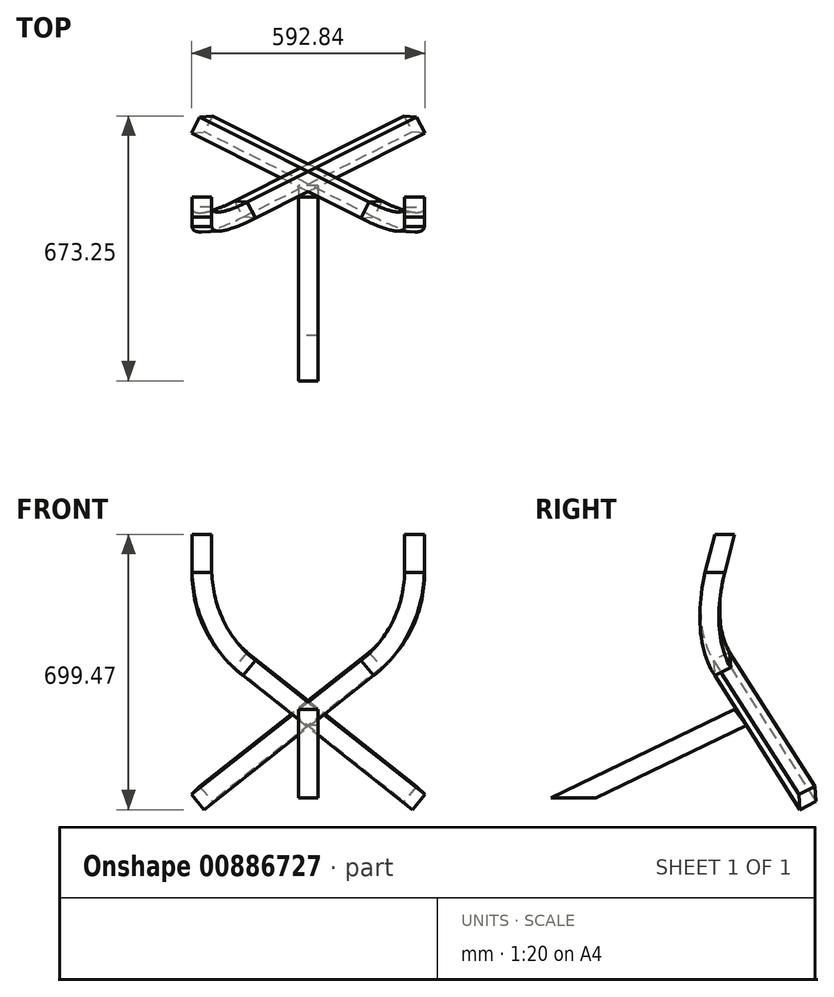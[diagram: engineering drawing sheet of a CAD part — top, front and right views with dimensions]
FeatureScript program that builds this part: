
annotation { "Feature Type Name" : "Feature", "Feature Type Description" : "" }
export const myFeature = defineFeature(function(context is Context, id is Id, definition is map)
    precondition{}
    {
        {
            var Q0;
            Q0=qCreatedBy(makeId("Top.planeOp"),FACE);
            var sketch = newSketch(context, id + "F0", { "sketchPlane" : qUnion([Q0])});
            skPoint(sketch, "E0", {"position": v(270, -243.58) * mm});
            skPoint(sketch, "E1", {"position": v(270, 136.42) * mm});
            skPoint(sketch, "E2", {"position": v(270, -73.58) * mm});
            skLineSegment(sketch, "E3", {"start": v(0, 0) * mm, "end": v(0, 375.12) * mm});
            skPoint(sketch, "E4.MirrorP", {"position": v(-270, 136.42) * mm});
            skPoint(sketch, "E5.MirrorP", {"position": v(-270, -73.58) * mm});
            skPoint(sketch, "E6.MirrorP", {"position": v(-270, -243.58) * mm});
            skLineSegment(sketch, "E7.bottom", {"start": v(-295, 111.42) * mm, "end": v(-245, 111.42) * mm});
            skLineSegment(sketch, "E7.top", {"start": v(-295, 161.42) * mm, "end": v(-245, 161.42) * mm});
            skLineSegment(sketch, "E7.left", {"start": v(-295, 111.42) * mm, "end": v(-295, 161.42) * mm});
            skLineSegment(sketch, "E7.right", {"start": v(-245, 111.42) * mm, "end": v(-245, 161.42) * mm});
            skPoint(sketch, "E8", {"position": v(0, -400) * mm});
            skSolve(sketch);
        }
        {
            var Q0;
            Q0=qCreatedBy(makeId("Top.planeOp"),FACE);
            cPlane(context, id + "F1", {"entities" : qUnion([Q0]), "cplaneType" : CPlaneType.OFFSET, "offset" : 670 * mm, "width" : 150 * mm, "height" : 150 * mm});
        }
        {
            var Q0;
            Q0=qCreatedBy(id+"F1.planeOp",FACE);
            var sketch = newSketch(context, id + "F2", { "sketchPlane" : qUnion([Q0])});
            skPoint(sketch, "E9.0", {"position": v(270, -73.58) * mm});
            skPoint(sketch, "E10.0", {"position": v(-270, -73.58) * mm});
            skLineSegment(sketch, "E11.bottom", {"start": v(245, -48.58) * mm, "end": v(295, -48.58) * mm});
            skLineSegment(sketch, "E11.top", {"start": v(245, -98.58) * mm, "end": v(295, -98.58) * mm});
            skLineSegment(sketch, "E11.left", {"start": v(245, -48.58) * mm, "end": v(245, -98.58) * mm});
            skLineSegment(sketch, "E11.right", {"start": v(295, -48.58) * mm, "end": v(295, -98.58) * mm});
            skSolve(sketch);
        }
        {
            var Q0;
            Q0=sQuery(id+"F0.wireOp",VERTEX,"E0");
            var Q1;
            Q1=sQuery(id+"F0.wireOp",VERTEX,"E4.MirrorP");
            var Q2;
            Q2=sQuery(id+"F2.wireOp",VERTEX,"E9.0");
            cPlane(context, id + "F3", {"entities" : qUnion([Q0, Q1, Q2]), "cplaneType" : CPlaneType.THREE_POINT, "offset" : 25 * mm, "width" : 150 * mm, "height" : 150 * mm});
        }
        {
            var Q0;
            Q0=qCreatedBy(id+"F3.planeOp",FACE);
            var sketch = newSketch(context, id + "F4", { "sketchPlane" : qUnion([Q0])});
            skPoint(sketch, "E12.0", {"position": v(-297.57, 33.55) * mm});
            skPoint(sketch, "E13.0", {"position": v(356.09, 631.33) * mm});
            skPoint(sketch, "E14.0", {"position": v(356.09, -59.9) * mm});
            skLineSegment(sketch, "E15", {"start": v(-297.57, 33.55) * mm, "end": v(223.46, 310.6) * mm});
            skLineSegment(sketch, "E16", {"start": v(356.09, 531.33) * mm, "end": v(356.09, 631.33) * mm});
            skPoint(sketch, "E17.visualSharp", {"position": v(356.09, 381.11) * mm});
            skArc(sketch, "E17.filletArc", {"start": v(223.46, 310.6) * mm, "mid": v(320.38, 402.57) * mm, "end": v(356.09, 531.33) * mm});
            skSolve(sketch);
        }
        {
            var Q0;
            Q0=makeQuery(id+"F2.imprint","IMPRINT",FACE,{"disambiguationData":[TD([[makeQuery(id+"F2.imprint","IMPRINT",EDGE,{"derivedFrom":sQuery(id+"F2.wireOp",EDGE,"E11.bottom")}),-1.0]])]});
            var Q1;
            Q1=sQuery(id+"F4.wireOp",EDGE,"E16");
            var Q2;
            Q2=sQuery(id+"F4.wireOp",EDGE,"E17.filletArc");
            var Q3;
            Q3=sQuery(id+"F4.wireOp",EDGE,"E15");
            sweep(context, id + "F5", {"profiles" : qUnion([Q0]), "path" : qUnion([Q1, Q2, Q3])});
        }
        {
            var Q0;
            Q0=makeQuery(id+"F5.opSweep","SWEPT_BODY",BODY,{"disambiguationData":[OSD([sQuery(id+"F2.wireOp",EDGE,"E11.bottom"),sQuery(id+"F2.wireOp",EDGE,"E11.top"),sQuery(id+"F2.wireOp",EDGE,"E11.left"),sQuery(id+"F2.wireOp",EDGE,"E11.right"),sQuery(id+"F4.wireOp",EDGE,"E15")])]});
            var Q1;
            Q1=qCreatedBy(makeId("Right.planeOp"),FACE);
            mirror(context, id + "F6", {"entities" : qUnion([Q0]), "mirrorPlane" : qUnion([Q1])});
        }
        {
            var Q0;
            Q0=qCreatedBy(makeId("Right.planeOp"),FACE);
            var sketch = newSketch(context, id + "F7", { "sketchPlane" : qUnion([Q0])});
            skPoint(sketch, "E18.0", {"position": v(-400, 0) * mm});
            skLineSegment(sketch, "E19", {"start": v(-400, 0) * mm, "end": v(-18.6, 183.98) * mm});
            skLineSegment(sketch, "E20", {"start": v(-18.6, 183.98) * mm, "end": v(-48.2, 225.21) * mm});
            skLineSegment(sketch, "E21", {"start": v(-48.2, 225.21) * mm, "end": v(-515.08, 0) * mm});
            skLineSegment(sketch, "E22", {"start": v(-515.08, 0) * mm, "end": v(-400, 0) * mm});
            skSolve(sketch);
        }
        {
            var Q0;
            Q0 = qSketchRegion(id + "F7", true);
            extrude(context, id + "F8", {"entities" : qUnion([Q0]), "endBound" : BoundingType.SYMMETRIC, "depth" : 50 * mm, "offsetDistance" : 25 * mm});
        }
    });
